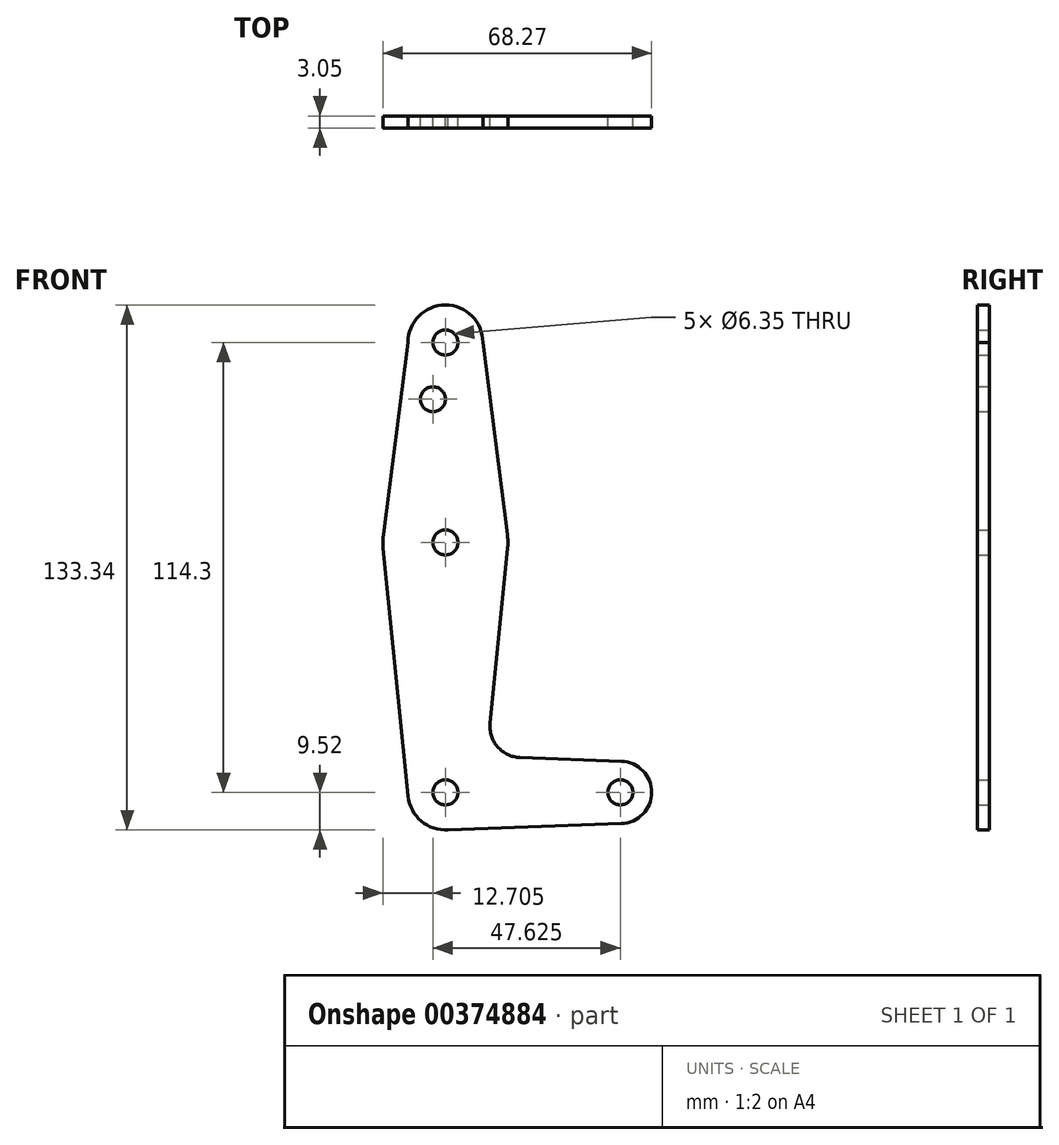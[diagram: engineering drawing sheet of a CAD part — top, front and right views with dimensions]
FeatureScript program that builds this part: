
annotation { "Feature Type Name" : "Feature", "Feature Type Description" : "" }
export const myFeature = defineFeature(function(context is Context, id is Id, definition is map)
    precondition{}
    {
        {
            var Q0;
            Q0=qCreatedBy(makeId("Front.planeOp"),FACE);
            var sketch = newSketch(context, id + "F0", { "sketchPlane" : qUnion([Q0])});
            skLineSegment(sketch, "E0", {"start": v(0, -114.3) * mm, "end": v(44.45, -114.3) * mm, "construction": true});
            skCircle(sketch, "E1", {"center": v(0, 0) * mm, "radius": 9.53 * mm});
            skCircle(sketch, "E2", {"center": v(44.45, -114.3) * mm, "radius": 7.94 * mm});
            skCircle(sketch, "E3", {"center": v(0, -114.3) * mm, "radius": 9.53 * mm});
            skLineSegment(sketch, "E4.trimOffspring", {"start": v(0, 0) * mm, "end": v(0, -114.3) * mm, "construction": true});
            skLineSegment(sketch, "E5", {"start": v(9.53, 0) * mm, "end": v(9.53, 0) * mm});
            skLineSegment(sketch, "E6", {"start": v(15.8, -52.39) * mm, "end": v(11.34, -96.7) * mm});
            skLineSegment(sketch, "E7", {"start": v(0, -123.82) * mm, "end": v(44.73, -122.23) * mm});
            skPoint(sketch, "E8.orphan", {"position": v(-9.53, 0) * mm});
            skLineSegment(sketch, "E9", {"start": v(-9.53, 0) * mm, "end": v(-15.75, -48.8) * mm});
            skCircle(sketch, "E10.converted", {"center": v(0, -50.8) * mm, "radius": 15.88 * mm});
            skLineSegment(sketch, "E11", {"start": v(-15.8, -52.39) * mm, "end": v(-9.48, -115.25) * mm});
            skLineSegment(sketch, "E12", {"start": v(9.53, 0) * mm, "end": v(15.75, -48.8) * mm});
            skCircle(sketch, "E13", {"center": v(0, -114.3) * mm, "radius": 3.18 * mm});
            skCircle(sketch, "E14", {"center": v(0, -50.8) * mm, "radius": 3.18 * mm});
            skCircle(sketch, "E15", {"center": v(44.45, -114.3) * mm, "radius": 3.18 * mm});
            skCircle(sketch, "E16", {"center": v(0, 0) * mm, "radius": 3.18 * mm});
            skCircle(sketch, "E17", {"center": v(-3.18, -14.41) * mm, "radius": 3.18 * mm});
            skLineSegment(sketch, "E18", {"start": v(18.97, -105.45) * mm, "end": v(44.73, -106.37) * mm});
            skArc(sketch, "E19.filletArc", {"start": v(11.34, -96.7) * mm, "mid": v(13.26, -102.73) * mm, "end": v(18.97, -105.45) * mm});
            skSolve(sketch);
        }
        {
            var Q0;
            Q0 = qSketchRegion(id + "F0", true);
            extrude(context, id + "F1", {"entities" : qUnion([Q0]), "depth" : 3.05 * mm});
        }
    });
